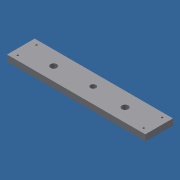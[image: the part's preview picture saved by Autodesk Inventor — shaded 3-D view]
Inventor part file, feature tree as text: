
AUTODESK INVENTOR PART (.ipt)
format: ipt  version: 2018 (Build 220112000, 112)  size: 94,208 bytes
history: native  units: mm
features: extrude x1, sketch x1
ambient origin geometry x8: Origin, YZ Plane, XZ Plane, XY Plane, X Axis, Y Axis, Z Axis, Center Point
bodies: Solid1 (feature_tree)
feature tree (2):
  extrude  "Extrusion1"  Depth=225.0mm
  sketch  "Sketch1"  dims[d0=45.0mm d1=225.0mm d2=30.0mm d3=3.0mm d4=3.0mm d5=7.5mm d6=7.5mm d7=3.0mm d8=3.0mm d9=30.0mm d10=10.0mm d11=10.0mm d12=10.0mm d13=0.0mm]
